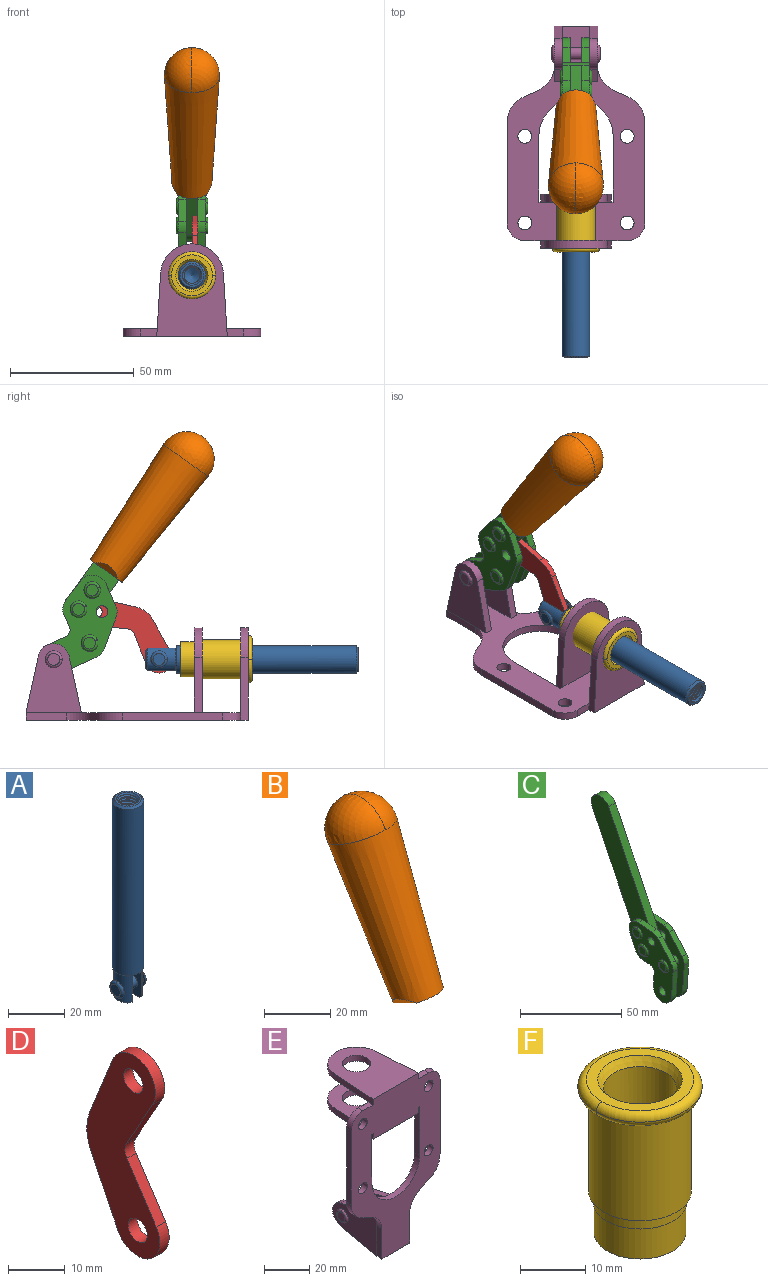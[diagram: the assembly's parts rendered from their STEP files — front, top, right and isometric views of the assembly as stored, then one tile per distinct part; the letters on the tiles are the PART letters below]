
ASSEMBLY  parts=6 mates=5
PART A: 48 faces, bbox 12.6x11.1x86.1 mm
  f0: torus R=2.41mm, axis (-1,0,0), area 15mm2, adj f30,f32,f34
  f1: torus R=2.41mm, axis (-1,0,0), area 15mm2, adj f29,f31,f33
  f2: cylinder r=5.54mm len=72.39mm, axis (0,0,1), area 2518.5mm2, adj f3,f4,f42,f43
  f3: cone r=5.54mm half-angle=45deg, axis (0,0,1), area 7.6mm2, adj f2,f5,f41
  f4: cone r=5.54mm half-angle=45deg, axis (0,0,-1), area 34.9mm2, adj f2,f39
  f5: cylinder r=5.08mm len=11.48mm, axis (0,0,1), area 108.3mm2, adj f3,f7,f8,f41
  f6: cylinder r=2.41mm len=4.83mm, axis (-1,0,0), area 71.2mm2, adj f40,f41
  f7: cylinder r=2.41mm len=4.83mm, axis (-1,0,0), area 7.6mm2, adj f5,f34
  f8: cone r=5.08mm half-angle=45deg, axis (0,0,1), area 10.6mm2, adj f5,f37,f41
  f9: cone r=3.98mm half-angle=45deg, axis (0,0,1), area 17.6mm2, adj f27,f39,f45,f46,f47
  f10: cylinder r=2.41mm len=4.83mm, axis (-1,0,0), area 7.6mm2, adj f33,f38
  f11: cylinder r=3.2mm len=6.4mm, axis (0,0,1), area 78.4mm2, adj f12,f28,f44,f45,f47
  f12: cylinder r=3.2mm len=6.4mm, axis (0,0,1), area 10.5mm2, adj f11,f13,f45,f47
  f13: cylinder r=3.2mm len=6.4mm, axis (0,0,1), area 10.5mm2, adj f12,f14,f45,f47
  f14: cylinder r=3.2mm len=6.4mm, axis (0,0,1), area 10.5mm2, adj f13,f15,f45,f47
  f15: cylinder r=3.2mm len=6.4mm, axis (0,0,1), area 10.5mm2, adj f14,f16,f45,f47
  f16: cylinder r=3.2mm len=6.4mm, axis (0,0,1), area 10.5mm2, adj f15,f17,f45,f47
  f17: cylinder r=3.2mm len=6.4mm, axis (0,0,1), area 10.5mm2, adj f16,f18,f45,f47
  f18: cylinder r=3.2mm len=6.4mm, axis (0,0,1), area 10.5mm2, adj f17,f19,f45,f47
  f19: cylinder r=3.2mm len=6.4mm, axis (0,0,1), area 10.5mm2, adj f18,f20,f45,f47
  f20: cylinder r=3.2mm len=6.4mm, axis (0,0,1), area 10.5mm2, adj f19,f21,f45,f47
  f21: cylinder r=3.2mm len=6.4mm, axis (0,0,1), area 10.5mm2, adj f20,f22,f45,f47
  f22: cylinder r=3.2mm len=6.4mm, axis (0,0,1), area 10.5mm2, adj f21,f23,f45,f47
  f23: cylinder r=3.2mm len=6.4mm, axis (0,0,1), area 10.5mm2, adj f22,f24,f45,f47
  f24: cylinder r=3.2mm len=6.4mm, axis (0,0,1), area 10.5mm2, adj f23,f25,f45,f47
  f25: cylinder r=3.2mm len=6.4mm, axis (0,0,1), area 10.5mm2, adj f24,f26,f45,f47
  f26: cylinder r=3.2mm len=6.4mm, axis (0,0,1), area 10.5mm2, adj f25,f27,f45,f47
  f27: cylinder r=3.2mm len=6.4mm, axis (0,0,1), area 7.4mm2, adj f9,f26,f45,f47
  f28: cone r=3.2mm half-angle=60deg, axis (0,0,1), area 37.2mm2, adj f11
  f29: plane 4.83x4.83mm, normal (-1,0,0), area 18.3mm2, adj f1,f31
  f30: plane 4.83x4.83mm, normal (1,0,0), area 18.3mm2, adj f0,f32
  f31: torus R=2.41mm, axis (-1,0,0), area 15mm2, adj f1,f29,f33
  f32: torus R=2.41mm, axis (-1,0,0), area 15mm2, adj f0,f30,f34
  f33: plane 6.83x6.83mm, normal (1,0,0), area 18.3mm2, adj f1,f10,f31
  f34: plane 6.83x6.83mm, normal (-1,0,0), area 18.3mm2, adj f0,f7,f32
  f35: cone r=5.08mm half-angle=45deg, axis (0,0,1), area 10.6mm2, adj f36,f38,f40
  f36: plane 7.25x1.97mm, normal (0,0,-1), area 10mm2, adj f35,f40
  f37: plane 7.25x1.97mm, normal (0,0,-1), area 10mm2, adj f8,f41
  f38: cylinder r=5.08mm len=11.48mm, axis (0,0,1), area 108.3mm2, adj f10,f35,f40,f42
  f39: plane 9.55x9.55mm, normal (0,0,1), area 22mm2, adj f4,f9
  f40: plane 12.76x10.09mm, normal (1,0,0), area 95.7mm2, adj f6,f35,f36,f38,f42,f43
  f41: plane 12.76x10.09mm, normal (-1,0,0), area 95.7mm2, adj f3,f5,f6,f8,f37,f43
  f42: cone r=5.54mm half-angle=45deg, axis (0,0,1), area 7.6mm2, adj f2,f38,f40
  f43: plane 11.07x4.7mm, normal (0,0,-1), area 50.4mm2, adj f2,f40,f41
  f44: plane 0.89x0.62mm, normal (-1,0,0), area 0.3mm2, adj f11,f45,f46,f47
  f45: bspline ~24.8x7.63mm, area 266.6mm2, adj f9,f11,f12,f13,f14,f15,f16,f17
  f46: bspline ~24.87x7.63mm, area 73.6mm2, adj f9,f44,f45,f47
  f47: bspline ~24.98x7.63mm, area 272.5mm2, adj f9,f11,f12,f13,f14,f15,f16,f17
PART B: 11 faces, bbox 22.3x42.6x64.5 mm
  f0: sphere r=11.13mm, area 411.4mm2, adj f1,f8
  f1: cone r=11.11mm half-angle=3.3deg, axis (0,0.44,0.9), area 3251.8mm2, adj f0,f7,f8,f9,f10
  f2: cylinder r=6.16mm len=11.7mm, axis (1,0,0), area 89.5mm2, adj f3,f4,f5,f6
  f3: plane 60.23x36.75mm, normal (-1,0,0), area 763.6mm2, adj f2,f4,f6,f10
  f4: plane 51.37x25.05mm, normal (0,0.9,-0.44), area 264.2mm2, adj f2,f3,f5,f10
  f5: plane 60.23x36.75mm, normal (1,0,0), area 763.6mm2, adj f2,f4,f6,f10
  f6: plane 51.37x25.05mm, normal (0,-0.9,0.44), area 264.2mm2, adj f2,f3,f5,f10
  f7: plane 9.95x5.95mm, normal (0.71,-0.31,-0.64), area 25.8mm2, adj f1,f10
  f8: sphere r=11.13mm, area 411.4mm2, adj f0,f1
  f9: plane 9.95x5.95mm, normal (-0.71,-0.31,-0.64), area 25.8mm2, adj f1,f10
  f10: plane 14.27x11.38mm, normal (0,-0.44,-0.9), area 106.7mm2, adj f1,f3,f4,f5,f6,f7,f9
PART C: 59 faces, bbox 12.9x60.2x99.6 mm
  f0: torus R=2.39mm, axis (-1,0,0), area 14.9mm2, adj f20,f43,f51
  f1: torus R=2.39mm, axis (-1,0,0), area 14.9mm2, adj f19,f42,f51
  f2: torus R=2.39mm, axis (-1,0,0), area 14.9mm2, adj f18,f35,f51
  f3: torus R=2.39mm, axis (-1,0,0), area 14.9mm2, adj f14,f17,f23
  f4: torus R=2.39mm, axis (-1,0,0), area 14.9mm2, adj f13,f16,f23
  f5: torus R=2.39mm, axis (-1,0,0), area 14.9mm2, adj f12,f15,f23
  f6: cylinder r=2.39mm len=4.78mm, axis (1,0,0), area 46.5mm2, adj f48,f50,f51
  f7: cylinder r=2.39mm len=4.78mm, axis (1,0,0), area 46.5mm2, adj f50,f51
  f8: cylinder r=6.35mm len=12.68mm, axis (1,0,0), area 61.8mm2, adj f38,f39,f50,f51
  f9: cylinder r=2.39mm len=4.78mm, axis (-1,0,0), area 70.5mm2, adj f46,f50
  f10: cylinder r=2.39mm len=4.78mm, axis (-1,0,0), area 46.5mm2, adj f23,f45,f46
  f11: cylinder r=2.39mm len=4.78mm, axis (-1,0,0), area 46.5mm2, adj f23,f46
  f12: plane 4.78x4.78mm, normal (1,0,0), area 17.9mm2, adj f5,f15
  f13: plane 4.78x4.78mm, normal (1,0,0), area 17.9mm2, adj f4,f16
  f14: plane 4.78x4.78mm, normal (1,0,0), area 17.9mm2, adj f3,f17
  f15: torus R=2.39mm, axis (-1,0,0), area 14.9mm2, adj f5,f12,f23
  f16: torus R=2.39mm, axis (-1,0,0), area 14.9mm2, adj f4,f13,f23
  f17: torus R=2.39mm, axis (-1,0,0), area 14.9mm2, adj f3,f14,f23
  f18: plane 4.78x4.78mm, normal (-1,0,0), area 17.9mm2, adj f2,f35
  f19: plane 4.78x4.78mm, normal (-1,0,0), area 17.9mm2, adj f1,f42
  f20: plane 4.78x4.78mm, normal (-1,0,0), area 17.9mm2, adj f0,f43
  f21: plane 2.26x0.2mm, normal (1,0,0), area 0.2mm2, adj f31,f44
  f22: plane 2.26x0.2mm, normal (-1,0,0), area 0.2mm2, adj f41,f44
  f23: plane 39.37x30.77mm, normal (1,0,0), area 565.5mm2, adj f3,f4,f5,f10,f11,f15,f16,f17
  f24: cylinder r=6.1mm len=4.15mm, axis (-1,0,0), area 14.7mm2, adj f23,f25,f32,f46
  f25: plane 10.25x9.01mm, normal (0,-0.75,0.66), area 42.3mm2, adj f23,f24,f26,f46
  f26: cylinder r=6.35mm len=4.64mm, axis (-1,0,0), area 15.6mm2, adj f23,f25,f27,f46
  f27: plane 15.84x3.1mm, normal (0,-1,-0.07), area 49.2mm2, adj f23,f26,f28,f46
  f28: cylinder r=6.35mm len=12.68mm, axis (-1,0,0), area 61.8mm2, adj f23,f27,f29,f46
  f29: plane 8.11x3.1mm, normal (0,1,0.07), area 25.2mm2, adj f23,f28,f30,f46
  f30: cylinder r=3.05mm len=3.25mm, axis (-1,0,0), area 14.8mm2, adj f23,f29,f31,f46
  f31: plane 5.99x3.1mm, normal (0,0.07,-1), area 18.6mm2, adj f21,f23,f30,f44,f46
  f32: plane 9.5x3.1mm, normal (0,-0.07,1), area 29.5mm2, adj f23,f24,f33,f46,f47
  f33: cylinder r=6.1mm len=8.63mm, axis (-1,0,0), area 39.1mm2, adj f23,f32,f34,f47
  f34: plane 8.65x3.96mm, normal (0,0.91,-0.42), area 29.5mm2, adj f23,f33,f44,f47
  f35: torus R=2.39mm, axis (-1,0,0), area 14.9mm2, adj f2,f18,f51
  f36: plane 10.25x9.01mm, normal (0,-0.75,0.66), area 42.3mm2, adj f37,f49,f50,f51
  f37: cylinder r=6.35mm len=4.64mm, axis (1,0,0), area 15.6mm2, adj f36,f38,f50,f51
  f38: plane 15.84x3.1mm, normal (0,-1,-0.07), area 49.2mm2, adj f8,f37,f50,f51
  f39: plane 8.11x3.1mm, normal (0,1,0.07), area 25.2mm2, adj f8,f40,f50,f51
  f40: cylinder r=3.05mm len=3.25mm, axis (1,0,0), area 14.8mm2, adj f39,f41,f50,f51
  f41: plane 5.99x3.1mm, normal (0,0.07,-1), area 18.6mm2, adj f22,f40,f44,f50,f51
  f42: torus R=2.39mm, axis (-1,0,0), area 14.9mm2, adj f1,f19,f51
  f43: torus R=2.39mm, axis (-1,0,0), area 14.9mm2, adj f0,f20,f51
  f44: cylinder r=6.35mm len=12.12mm, axis (-1,0,0), area 128.9mm2, adj f21,f22,f23,f31,f34,f41,f46,f47
  f45: plane 2.65x1.35mm, normal (1,0,0), area 1mm2, adj f10,f55
  f46: plane 39.08x20.42mm, normal (-1,0,0), area 412.5mm2, adj f9,f10,f11,f24,f25,f26,f27,f28
  f47: plane 77.62x39.82mm, normal (1,0,0), area 850mm2, adj f32,f33,f34,f44,f53,f54,f55
  f48: plane 2.65x1.35mm, normal (-1,0,0), area 1mm2, adj f6,f55
  f49: cylinder r=6.1mm len=4.15mm, axis (1,0,0), area 14.7mm2, adj f36,f50,f51,f56
  f50: plane 39.08x20.42mm, normal (1,0,0), area 412.5mm2, adj f6,f7,f8,f9,f36,f37,f38,f39
  f51: plane 39.37x30.77mm, normal (-1,0,0), area 565.5mm2, adj f0,f1,f2,f6,f7,f8,f35,f36
  f52: plane 8.65x3.96mm, normal (0,0.91,-0.42), area 29.5mm2, adj f44,f51,f57,f58
  f53: plane 68.49x33.4mm, normal (0,0.9,-0.44), area 358.1mm2, adj f44,f47,f54,f58
  f54: cylinder r=6.35mm len=12.06mm, axis (1,0,0), area 93.7mm2, adj f47,f53,f55,f58
  f55: plane 68.49x33.4mm, normal (0,-0.9,0.44), area 358.1mm2, adj f44,f45,f46,f47,f48,f50,f54,f58
  f56: plane 9.5x3.1mm, normal (0,-0.07,1), area 29.5mm2, adj f49,f50,f51,f57,f58
  f57: cylinder r=6.1mm len=8.63mm, axis (1,0,0), area 39.1mm2, adj f51,f52,f56,f58
  f58: plane 77.62x39.82mm, normal (-1,0,0), area 850mm2, adj f44,f52,f53,f54,f55,f56,f57
PART D: 12 faces, bbox 2.3x18.2x42.8 mm
  f0: cylinder r=2.4mm len=4.8mm, axis (1,0,0), area 34.9mm2, adj f4,f11
  f1: cylinder r=10.41mm len=8.47mm, axis (1,0,0), area 20.2mm2, adj f4,f9,f10,f11
  f2: cylinder r=3.05mm len=3.16mm, axis (1,0,0), area 7.7mm2, adj f4,f6,f7,f11
  f3: cylinder r=2.4mm len=4.8mm, axis (1,0,0), area 34.9mm2, adj f4,f11
  f4: plane 42.81x18.23mm, normal (-1,0,0), area 414.1mm2, adj f0,f1,f2,f3,f5,f6,f7,f8
  f5: cylinder r=5.54mm len=10.67mm, axis (1,0,0), area 41.8mm2, adj f4,f6,f10,f11
  f6: plane 11.66x6.53mm, normal (0,-0.87,-0.49), area 30.9mm2, adj f2,f4,f5,f11
  f7: plane 11.17x7.33mm, normal (0,-0.84,0.55), area 30.9mm2, adj f2,f4,f8,f11
  f8: cylinder r=5.54mm len=10.51mm, axis (1,0,0), area 41.8mm2, adj f4,f7,f9,f11
  f9: plane 13.67x6.67mm, normal (0,0.9,-0.44), area 35.1mm2, adj f1,f4,f8,f11
  f10: plane 14.1x5.7mm, normal (0,0.93,0.37), area 35.1mm2, adj f1,f4,f5,f11
  f11: plane 42.81x18.23mm, normal (1,0,0), area 414.1mm2, adj f0,f1,f2,f3,f5,f6,f7,f8
PART E: 55 faces, bbox 55.7x37.4x89.8 mm
  f0: torus R=2.41mm, axis (-1,0,0), area 15mm2, adj f11,f15,f25
  f1: torus R=2.41mm, axis (-1,0,0), area 15mm2, adj f10,f12,f22
  f2: cylinder r=2.78mm len=5.56mm, axis (0,-1,0), area 54.2mm2, adj f30,f54
  f3: cylinder r=14.99mm len=29.97mm, axis (0,-1,0), area 145.9mm2, adj f30,f49,f53,f54
  f4: cylinder r=2.78mm len=5.56mm, axis (0,-1,0), area 54.2mm2, adj f30,f54
  f5: cylinder r=2.78mm len=5.56mm, axis (0,-1,0), area 54.2mm2, adj f30,f54
  f6: cylinder r=2.78mm len=5.56mm, axis (0,-1,0), area 54.2mm2, adj f30,f54
  f7: cylinder r=6.35mm len=12.7mm, axis (0,0,1), area 123.6mm2, adj f27,f51
  f8: cylinder r=6.35mm len=12.7mm, axis (0,0,-1), area 124.7mm2, adj f21,f35
  f9: cylinder r=2.41mm len=11.18mm, axis (-1,0,0), area 169.4mm2, adj f16,f19
  f10: plane 4.83x4.83mm, normal (1,0,0), area 18.3mm2, adj f1,f12
  f11: plane 4.83x4.83mm, normal (-1,0,0), area 18.3mm2, adj f0,f15
  f12: torus R=2.41mm, axis (-1,0,0), area 15mm2, adj f1,f10,f22
  f13: cylinder r=6.35mm len=12.41mm, axis (1,0,0), area 53.4mm2, adj f18,f19,f22,f23
  f14: cylinder r=6.35mm len=12.41mm, axis (-1,0,0), area 53.4mm2, adj f16,f17,f24,f25
  f15: torus R=2.41mm, axis (-1,0,0), area 15mm2, adj f0,f11,f25
  f16: plane 27.86x22.35mm, normal (1,0,0), area 425.4mm2, adj f9,f14,f17,f24,f30
  f17: plane 22.86x4.97mm, normal (0,0.21,0.98), area 72.5mm2, adj f14,f16,f25,f30
  f18: plane 22.86x4.97mm, normal (0,0.21,0.98), area 72.5mm2, adj f13,f19,f22,f30
  f19: plane 27.86x22.35mm, normal (-1,0,0), area 425.4mm2, adj f9,f13,f18,f23,f30
  f20: cylinder r=12.7mm len=25.35mm, axis (0,0,-1), area 119.8mm2, adj f21,f34,f35,f36
  f21: plane 34.21x28.07mm, normal (0,0,-1), area 702.4mm2, adj f8,f20,f30,f34,f36
  f22: plane 27.96x22.45mm, normal (1,0,0), area 407.2mm2, adj f1,f12,f13,f18,f23,f30,f42,f43
  f23: plane 22.86x4.97mm, normal (0,0.21,-0.98), area 72.5mm2, adj f13,f19,f22,f44
  f24: plane 22.86x4.97mm, normal (0,0.21,-0.98), area 72.5mm2, adj f14,f16,f25,f44
  f25: plane 27.86x22.35mm, normal (-1,0,0), area 407.1mm2, adj f0,f14,f15,f17,f24,f30,f45,f46
  f26: plane 3.1x0.95mm, normal (0,0,-1), area 2.7mm2, adj f30,f49,f50,f54
  f27: plane 34.21x28.07mm, normal (0,0,1), area 702.4mm2, adj f7,f28,f30,f50,f52
  f28: cylinder r=12.7mm len=25.35mm, axis (0,0,1), area 118.8mm2, adj f27,f50,f51,f52
  f29: plane 3.1x0.95mm, normal (0,0,-1), area 2.7mm2, adj f30,f52,f53,f54
  f30: plane 86.54x55.63mm, normal (0,1,0), area 2362.9mm2, adj f2,f3,f4,f5,f6,f16,f17,f18
  f31: plane 40.56x3.1mm, normal (-1,0,0), area 125.7mm2, adj f30,f32,f48,f54
  f32: cylinder r=7.11mm len=7.11mm, axis (0,-1,0), area 34.6mm2, adj f30,f31,f33,f54
  f33: plane 6.67x3.1mm, normal (0,0,1), area 20.4mm2, adj f30,f32,f34,f54
  f34: plane 25.39x3.13mm, normal (-1,0.06,0), area 79.5mm2, adj f20,f21,f33,f35,f54
  f35: plane 37.31x28.45mm, normal (0,0,1), area 789.9mm2, adj f8,f20,f34,f36,f54
  f36: plane 25.39x3.13mm, normal (1,0.06,0), area 79.5mm2, adj f20,f21,f35,f37,f54
  f37: plane 6.67x3.1mm, normal (0,0,1), area 20.4mm2, adj f30,f36,f38,f54
  f38: cylinder r=7.11mm len=7.11mm, axis (0,-1,0), area 34.6mm2, adj f30,f37,f39,f54
  f39: plane 40.56x3.1mm, normal (1,0,0), area 125.7mm2, adj f30,f38,f40,f54
  f40: cylinder r=11.18mm len=10.16mm, axis (0,-1,0), area 39.5mm2, adj f30,f39,f41,f54
  f41: plane 6.09x3.1mm, normal (0.42,0,-0.91), area 20.8mm2, adj f30,f40,f42,f54
  f42: cylinder r=11.18mm len=9.41mm, axis (0,-1,0), area 37.2mm2, adj f22,f30,f41,f43,f54
  f43: plane 16.5x3.1mm, normal (1,0,0), area 51.1mm2, adj f22,f42,f44,f54
  f44: plane 17.37x3.1mm, normal (0,0,-1), area 53.8mm2, adj f23,f24,f30,f43,f45,f54
  f45: plane 16.5x3.1mm, normal (-1,0,0), area 51.1mm2, adj f25,f44,f46,f54
  f46: cylinder r=11.18mm len=9.41mm, axis (0,-1,0), area 37.2mm2, adj f25,f30,f45,f47,f54
  f47: plane 6.09x3.1mm, normal (-0.42,0,-0.91), area 20.8mm2, adj f30,f46,f48,f54
  f48: cylinder r=11.18mm len=10.16mm, axis (0,-1,0), area 39.5mm2, adj f30,f31,f47,f54
  f49: plane 26.54x3.1mm, normal (-1,0,0), area 82.3mm2, adj f3,f26,f30,f54
  f50: plane 25.39x3.1mm, normal (1,0.06,0), area 78.8mm2, adj f26,f27,f28,f51,f54
  f51: plane 37.31x28.45mm, normal (0,0,-1), area 789.9mm2, adj f7,f28,f50,f52,f54
  f52: plane 25.39x3.1mm, normal (-1,0.06,0), area 78.8mm2, adj f27,f28,f29,f51,f54
  f53: plane 26.54x3.1mm, normal (1,0,0), area 82.3mm2, adj f3,f29,f30,f54
  f54: plane 89.66x55.63mm, normal (0,-1,0), area 2678.5mm2, adj f2,f3,f4,f5,f6,f26,f29,f31
PART F: 15 faces, bbox 20.6x20.6x28.7 mm
  f0: torus R=8.26mm, axis (0,0,1), area 56.8mm2, adj f1,f10,f12
  f1: torus R=8.26mm, axis (0,0,1), area 56.8mm2, adj f0,f6,f13
  f2: cylinder r=5.59mm len=25.91mm, axis (0,0,1), area 909.6mm2, adj f3,f4
  f3: cone r=6.86mm half-angle=45deg, axis (0,0,-1), area 70.2mm2, adj f2,f14
  f4: cone r=6.47mm half-angle=30deg, axis (0,0,1), area 66.7mm2, adj f2,f13
  f5: cylinder r=7.04mm len=14.07mm, axis (0,0,1), area 252.6mm2, adj f11,f14
  f6: torus R=8.26mm, axis (0,0,1), area 56.8mm2, adj f1,f12,f13
  f7: cylinder r=7.16mm len=14.33mm, axis (0,0,1), area 91.5mm2, adj f9,f11
  f8: cylinder r=7.86mm len=18.42mm, axis (0,0,1), area 909.6mm2, adj f9,f10
  f9: plane 15.72x15.72mm, normal (0,0,-1), area 33mm2, adj f7,f8
  f10: plane 16.51x16.51mm, normal (0,0,-1), area 19.9mm2, adj f0,f8,f12
  f11: plane 14.33x14.33mm, normal (0,0,-1), area 5.7mm2, adj f5,f7
  f12: torus R=8.26mm, axis (0,0,1), area 56.8mm2, adj f0,f6,f10
  f13: plane 16.51x16.51mm, normal (0,0,1), area 82.7mm2, adj f1,f4,f6
  f14: plane 14.07x14.07mm, normal (0,0,-1), area 7.8mm2, adj f3,f5
PLACE A rot(axis=(1,0,0),90deg) t=(0,5.08,0)mm
PLACE B rot(axis=(1,0,0),61.7deg) t=(-0.04,-7.83,18.13)mm
PLACE C rot(axis=(1,0,0),61.7deg) t=(0,-7.83,18.13)mm
PLACE D rot(axis=(0,0.46,0.89),180deg) t=(1.16,16.42,14.72)mm
PLACE E rot(axis=(1,0,0),90deg) t=(0,0,0)mm fixed
PLACE F rot(axis=(1,0,0),90deg) t=(0,1.02,0)mm
MATE fastened B.f2 <-> C.f54  axis (1,0,0) through (-2.35,-22.45,106.63)mm
MATE revolute D.f3 <-> A.f6  axis (-1,0,0) through (0,-10.4,24.61)mm
MATE fastened F.f2 <-> E.f7  axis (0,-1,0) through (0,-46.39,24.61)mm
MATE slider A.f2 <-> F.f2  axis (0,-1,0) through (0,-53.7,24.61)mm
MATE revolute C.f7 <-> E.f0  axis (-1,0,0) through (0,32.09,24.61)mm
